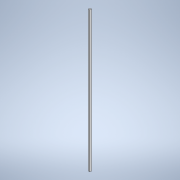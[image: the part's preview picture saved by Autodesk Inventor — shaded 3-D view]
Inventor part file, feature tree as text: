
AUTODESK INVENTOR PART (.ipt)
format: ipt  version: 2022 (Build 260153000, 153)  size: 149,504 bytes
history: native  units: mm
features: extrude x1, sketch x1
ambient origin geometry x8: Origin, YZ Plane, XZ Plane, XY Plane, X Axis, Y Axis, Z Axis, Center Point
bodies: Body1 (feature_tree)
feature tree (2):
  extrude  "Extrusion7"  Depth=5.0mm
  sketch  "Sketch4"  dims[d31=34.456mm d103=5.0mm d104=5.0mm d105=475.0mm d106=0.0mm]
